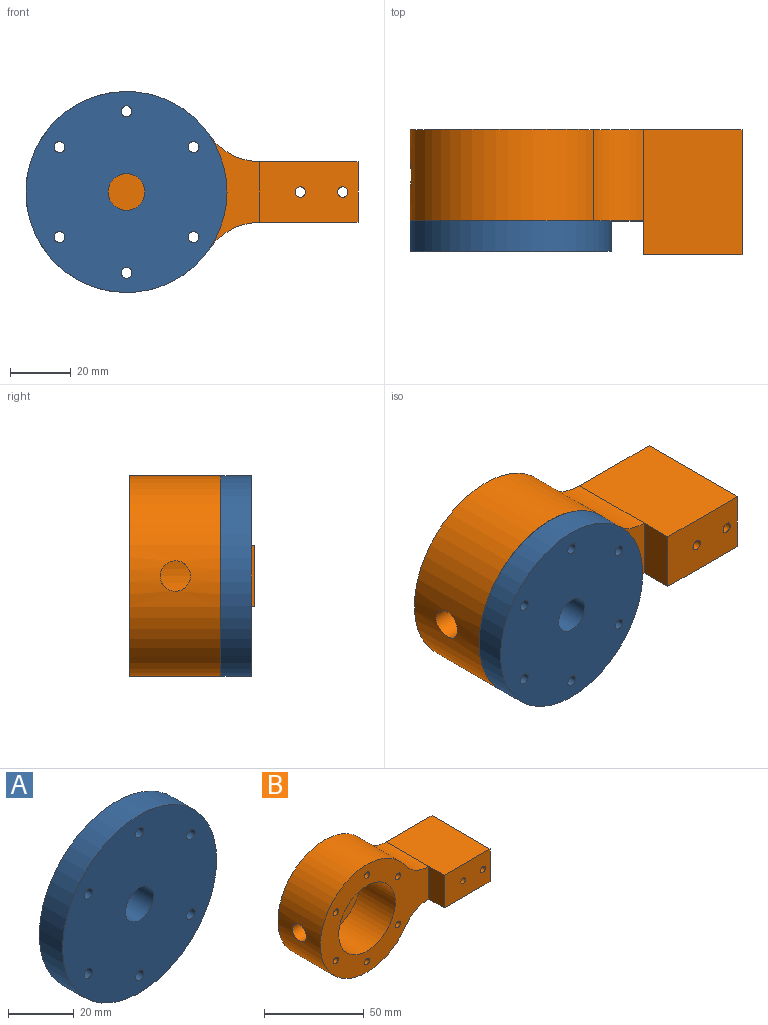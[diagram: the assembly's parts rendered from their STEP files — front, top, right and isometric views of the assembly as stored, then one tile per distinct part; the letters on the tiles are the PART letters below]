
ASSEMBLY  parts=2 mates=1
PART A: 10 faces, bbox 66x10x66 mm
  f0: cylinder r=6mm len=12mm, axis (0,1,0), area 377mm2, adj f2,f3
  f1: cylinder r=33mm len=66mm, axis (0,1,0), area 2073.5mm2, adj f2,f3
  f2: plane 66x66mm, normal (0,-1,0), area 3247mm2, adj f0,f1,f4,f5,f6,f7,f8,f9
  f3: plane 66x66mm, normal (0,1,0), area 3247mm2, adj f0,f1,f4,f5,f6,f7,f8,f9
  f4: cylinder r=1.8mm len=10mm, axis (0,1,0), area 113.1mm2, adj f2,f3
  f5: cylinder r=1.8mm len=10mm, axis (0,1,0), area 113.1mm2, adj f2,f3
  f6: cylinder r=1.8mm len=10mm, axis (0,1,0), area 113.1mm2, adj f2,f3
  f7: cylinder r=1.8mm len=10mm, axis (0,1,0), area 113.1mm2, adj f2,f3
  f8: cylinder r=1.8mm len=10mm, axis (0,1,0), area 113.1mm2, adj f2,f3
  f9: cylinder r=1.8mm len=10mm, axis (0,1,0), area 113.1mm2, adj f2,f3
PART B: 21 faces, bbox 109x41x66 mm
  f0: plane 41x32.31mm, normal (0,0,-1), area 1324.6mm2, adj f1,f2,f16,f18,f20
  f1: plane 32.31x20mm, normal (0,-1,0), area 628mm2, adj f0,f13,f17,f18,f19,f20
  f2: plane 109x66mm, normal (0,1,0), area 4256mm2, adj f0,f3,f7,f8,f9,f10,f11,f12
  f3: cylinder r=33mm len=66mm, axis (0,1,0), area 4950.2mm2, adj f2,f5,f14,f15,f16
  f4: cylinder r=20mm len=40mm, axis (0,1,0), area 3062.3mm2, adj f5,f6,f14
  f5: plane 76.69x66mm, normal (0,-1,0), area 2371.4mm2, adj f3,f4,f7,f8,f9,f10,f11,f12
  f6: plane 40x40mm, normal (0,-1,0), area 1256.6mm2, adj f4
  f7: cylinder r=1.8mm len=30mm, axis (0,-1,0), area 339.3mm2, adj f2,f5
  f8: cylinder r=1.8mm len=30mm, axis (0,-1,0), area 339.3mm2, adj f2,f5
  f9: cylinder r=1.8mm len=30mm, axis (0,-1,0), area 339.3mm2, adj f2,f5
  f10: cylinder r=1.8mm len=30mm, axis (0,-1,0), area 339.3mm2, adj f2,f5
  f11: cylinder r=1.8mm len=30mm, axis (0,-1,0), area 339.3mm2, adj f2,f5
  f12: cylinder r=1.8mm len=30mm, axis (0,-1,0), area 339.3mm2, adj f2,f5
  f13: plane 41x32.31mm, normal (0,0,1), area 1324.6mm2, adj f1,f2,f15,f18,f20
  f14: cylinder r=5mm len=13.64mm, axis (1,0,0), area 412.4mm2, adj f3,f4
  f15: cylinder r=20mm len=30mm, axis (0,1,0), area 581.5mm2, adj f2,f3,f5,f13
  f16: cylinder r=20mm len=30mm, axis (0,1,0), area 581.5mm2, adj f0,f2,f3,f5
  f17: cylinder r=1.7mm len=41mm, axis (0,-1,0), area 437.9mm2, adj f1,f2
  f18: plane 20x11mm, normal (-1,0,0), area 220mm2, adj f0,f1,f5,f13
  f19: cylinder r=1.7mm len=41mm, axis (0,-1,0), area 437.9mm2, adj f1,f2
  f20: plane 41x20mm, normal (1,0,0), area 820mm2, adj f0,f1,f2,f13
PLACE A t=(-10.07,-76.64,28.22)mm
PLACE B t=(-10.07,-46.64,28.22)mm
MATE fastened A.f6 <-> B.f10  axis (0,1,0) through (-32.07,-76.64,13.45)mm
